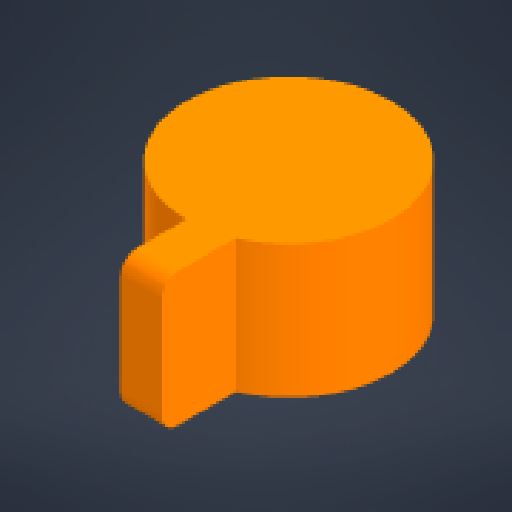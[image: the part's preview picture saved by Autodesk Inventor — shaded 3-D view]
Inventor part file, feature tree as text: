
AUTODESK INVENTOR PART (.ipt)
format: ipt  version: 2024 (Build 280153000, 153)  size: 231,424 bytes
history: native  units: mm
features: other x7, sketch x3, extrude x3, reference x3, fillet x1, mirror x1
ambient origin geometry x8: Origin, YZ Plane, XZ Plane, XY Plane, X Axis, Y Axis, Z Axis, Center Point
bodies: Body1 (feature_tree)
feature tree (18):
  other  "Твердое тело1"
  sketch  "Эскиз1"
  other  "РабПлоскость1"
  extrude  "Выдавливание1"  Depth=13.75mm TaperAngle=0.0deg
  sketch  "Эскиз2"
  other  "РабПлоскость2"
  extrude  "Выдавливание2"  Depth=10.0mm TaperAngle=0.0deg
  extrude  "Выдавливание3"  TaperAngle=0.0deg  [1 undecoded]
  fillet  "Сопряжение1"  Radius=2.0mm
  other  "РабПлоскость3"
  mirror  "Зеркальное отражение1"
  reference  "Ссылка1"
  sketch  "Эскиз3"
  reference  "Ссылка5"
  reference  "Ссылка6"
  parser-record x1  (decoder bookkeeping rows leaked as tree rows — omitted from the tree; the rows remain in map.json)
  other  "default_motor_asembly.iam"
  other  "lower_arm:1"
note: 1 required parameter value undecoded (feature->parameter linkage not recoverable at this tier; creation-order binding heuristic only, values carry confidence <= 0.55)
note: 1 file-system path scrubbed to <path> (originals preserved in map.json)
